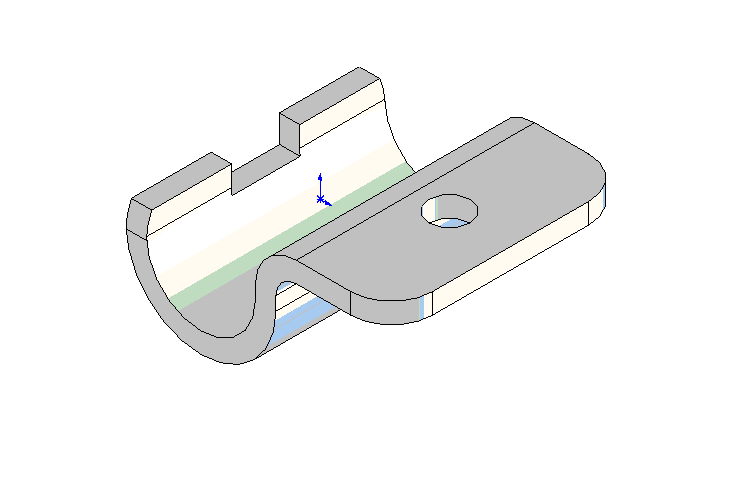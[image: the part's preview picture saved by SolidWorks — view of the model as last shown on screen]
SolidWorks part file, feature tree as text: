
SOLIDWORKS PART (.sldprt)
format: sldprt  version: not decoded by parser v0  size: 220,672 bytes
history: native  units: mm
features: sketch x4, plane x3, cut_extrude x3, material x1, extrude x1, fillet x1 (+10 scaffold rows collapsed)
feature tree (23):
  scaffold x10  (default folders/planes/origin — collapsed)
  material  "Matériau <non spécifié>"
  plane  "Plan de face"
  plane  "Plan de dessus"
  plane  "Plan de droite"
  sketch  "Esquisse1"  dims[D1=16.0mm D5=3.0mm D6=6.0mm D3=16.0mm D4=36.0mm D7=5.0mm D2=3.0mm]
  extrude  "Extrusion1"  Depth=35mm
  fillet  "Congé1"  Radius=6mm
  sketch  "Esquisse2"  dims[D1=6.0mm D2=30.0mm]
  cut_extrude  "Enlèv. mat.-Extru.1"  [1 undecoded]
  sketch  "Esquisse3"  dims[D1=17.0mm]
  cut_extrude  "Enlèv. mat.-Extru.6"  Depth=35mm
  sketch  "Esquisse4"  dims[D1=10.0mm D2=4.0mm]
  cut_extrude  "Enlèv. mat.-Extru.7"  [1 undecoded]
decode coverage: 7 of 9 modeling features carry decoded parameters
note: 2 parameter values undecoded
note: suppression state not decoded; provenance and decode notes live in map.json
